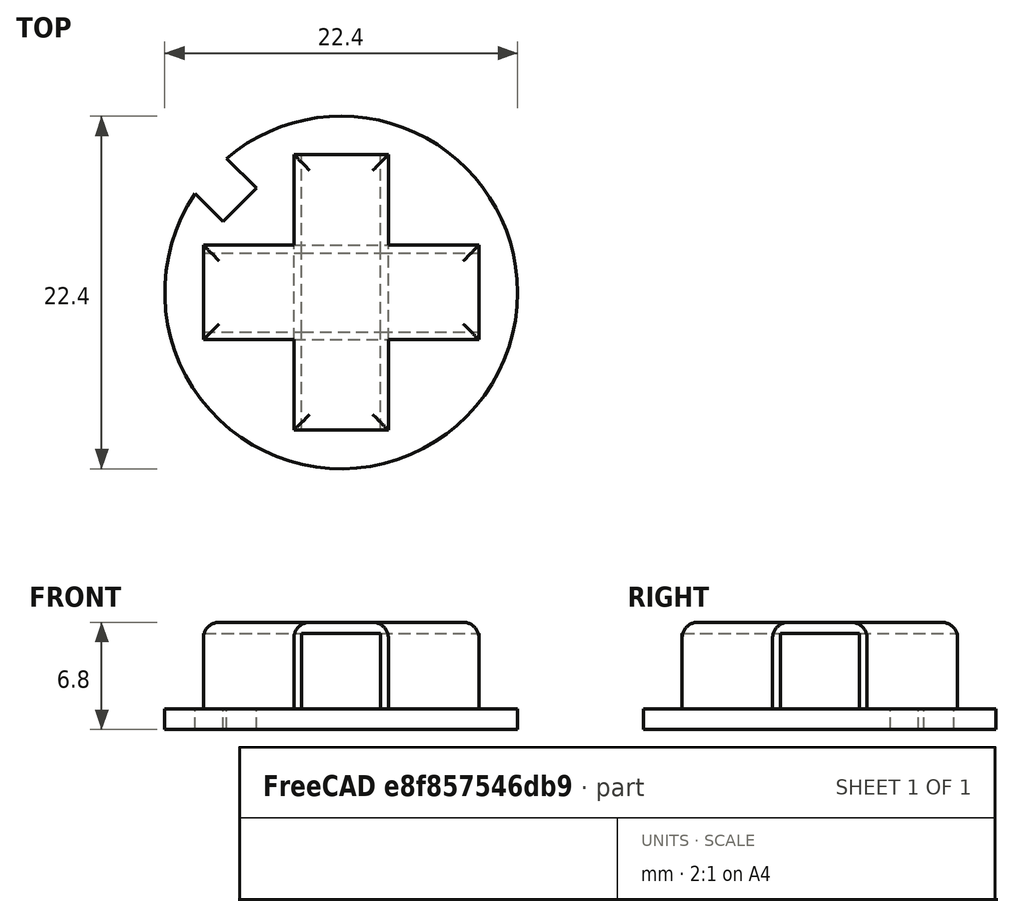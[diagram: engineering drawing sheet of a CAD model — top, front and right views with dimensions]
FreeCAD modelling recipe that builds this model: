
FCSTD DOCUMENT  (FreeCAD 0.18R16131 (Git))
Label: GBC_D_pad
License: All rights reserved
LicenseURL: http://en.wikipedia.org/wiki/All_rights_reserved
objects: Part::Box×8, Part::Fillet×2, Part::Cylinder×1, Part::Cut×1
note: 12 computed .brp shape members not serialized (recipe doc carries the construction recipe); baked Part::Feature solids carry a one-line shape summary decoded from their .brp

FEATURE [Part::Cylinder] Cylinder
  Angle = 360
  AttacherType = Attacher::AttachEngine3D
  Height = 1.3
  Placement = pos=(0,0,-1.3) rot=(0,0,1;0rad)
  Radius = 11.2
FEATURE [Part::Box] Box  label="Cube(dpad_vertical_top)"
  AttacherType = Attacher::AttachEngine3D
  Height = 4.8
  Length = 5
  Placement = pos=(-2.5,2.5,0) rot=(0,0,1;0rad)
  Width = 6.25
FEATURE [Part::Box] Box001  label="Cube(dpad_horizontal_left)"
  AttacherType = Attacher::AttachEngine3D
  Height = 4.8
  Length = 6.25
  Placement = pos=(-8.75,-2.5,0) rot=(0,0,1;0rad)
  Width = 5
FEATURE [Part::Box] Box002  label="Cube(corner_cut)"
  AttacherType = Attacher::AttachEngine3D
  Height = 10
  Length = 3
  Placement = pos=(-7.5,4.5,-1.3) rot=(0,0,1;0.785398rad)
  Width = 3
FEATURE [Part::Box] Box003  label="Cube(dpad_vertical_bottom)"
  AttacherType = Attacher::AttachEngine3D
  Height = 4.8
  Length = 5
  Placement = pos=(-2.5,-8.75,0) rot=(0,0,1;0rad)
  Width = 6.25
FEATURE [Part::Box] Box004  label="Cube(dpad_horizontal_right)"
  AttacherType = Attacher::AttachEngine3D
  Height = 4.8
  Length = 6.25
  Placement = pos=(2.5,-2.5,0) rot=(0,0,1;0rad)
  Width = 5
FEATURE [Part::Box] Box005  label="Cube(dpad_middle)"
  AttacherType = Attacher::AttachEngine3D
  Height = 4.8
  Length = 5
  Placement = pos=(-2.5,-2.5,0) rot=(0,0,1;0rad)
  Width = 5
FEATURE [Part::Box] Box006  label="Cube(dpad_horizontal_full)"
  AttacherType = Attacher::AttachEngine3D
  Height = 5.5
  Length = 17.5
  Placement = pos=(-8.75,-3,0) rot=(0,0,1;0rad)
  Width = 6
FEATURE [Part::Box] Box007  label="Cube(dpad_vertical_full)"
  AttacherType = Attacher::AttachEngine3D
  Height = 5.5
  Length = 6
  Placement = pos=(-3,-8.75,0) rot=(0,0,1;0rad)
  Width = 17.5
FEATURE [Part::Fillet] Fillet
  Base = -> Box007
  Edges = 4 edges r=1: [Edge2,Edge6,Edge10,Edge12]
FEATURE [Part::Fillet] Fillet001
  Base = -> Box006
  Edges = 4 edges r=1: [Edge2,Edge6,Edge10,Edge12]
FEATURE [Part::Cut] Cut
  Base = -> Cylinder
  Tool = -> Box002
